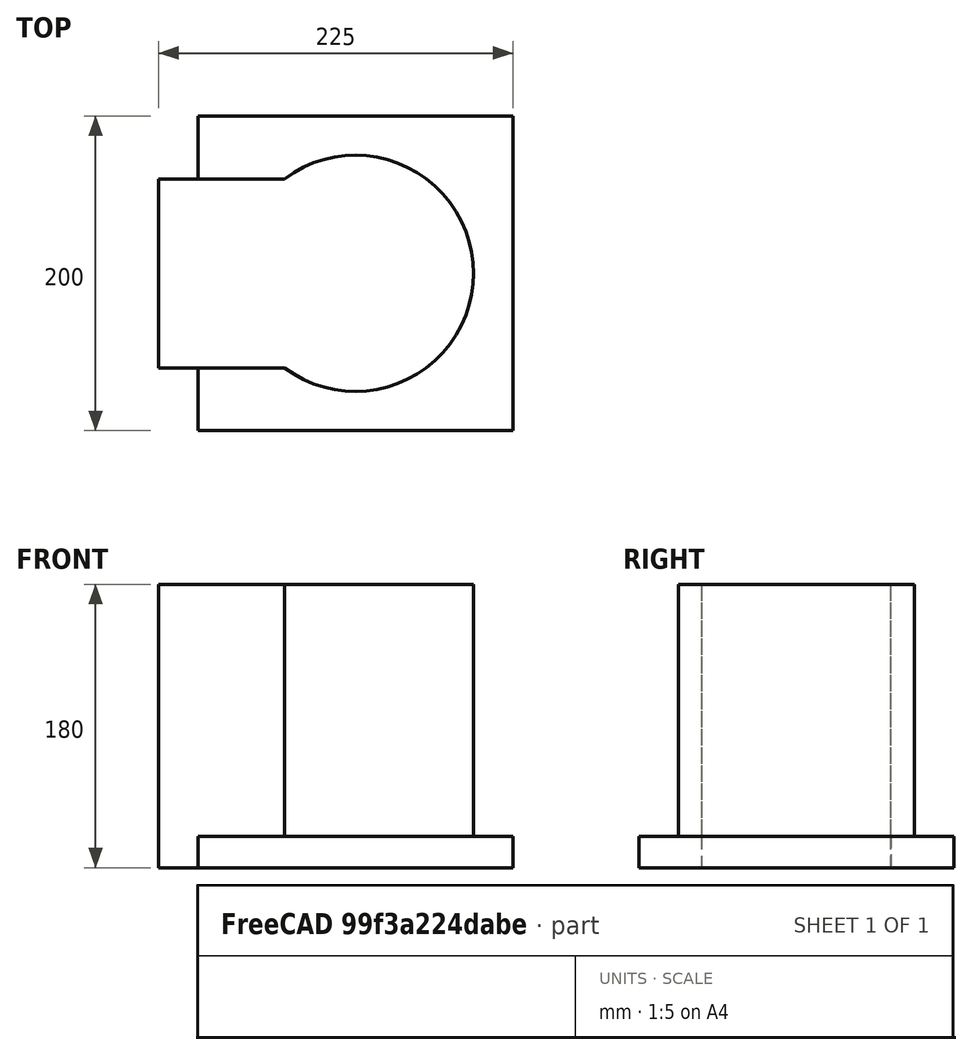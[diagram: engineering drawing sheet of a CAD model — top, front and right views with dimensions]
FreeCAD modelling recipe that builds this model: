
FCSTD DOCUMENT  (FreeCAD 0.19R)
Label: lk0
License: All rights reserved
LicenseURL: http://en.wikipedia.org/wiki/All_rights_reserved
objects: Sketcher::SketchObject×2, PartDesign::Pad×2, PartDesign::Body×1, Mesh::Feature×1
note: 7 computed .brp shape members not serialized (recipe doc carries the construction recipe); baked Part::Feature solids carry a one-line shape summary decoded from their .brp

FEATURE [Sketcher::SketchObject] Sketch
  FullyConstrained = true
  MapMode = 5
  Support = -> [XY_Plane]
  sketch-geometry (4):
    g0: ArcOfCircle CenterX=0 CenterY=0 CenterZ=0 NormalX=0 NormalY=0 NormalZ=1 AngleXU=0 Radius=75 StartAngle=4.06889 EndAngle=8.49748
    g1: LineSegment StartX=-45 StartY=60 StartZ=0 EndX=-125 EndY=60 EndZ=0
    g2: LineSegment StartX=-125 StartY=60 StartZ=0 EndX=-125 EndY=-60 EndZ=0
    g3: LineSegment StartX=-125 StartY=-60 StartZ=0 EndX=-45 EndY=-60 EndZ=0
  constraints (11):
    c: Coincident(g0,g-1)
    c: Diameter(g0) = 150
    c: Coincident(g1,g2)
    c: Coincident(g2,g3)
    c: Horizontal(g1)
    c: Horizontal(g3)
    c: DistanceY(g2,g2) = 120
    c: Symmetric(g1,g2,g-1)
    c: Coincident(g0,g3)
    c: Coincident(g0,g1)
    c: DistanceX(g1,g1) = 80
FEATURE [PartDesign::Pad] Pad
  Direction = (1,1,1)
  Length = 180
  Length2 = 100
  Profile = -> Sketch
  Type = 0
FEATURE [Sketcher::SketchObject] Sketch001
  FullyConstrained = true
  MapMode = 5
  Support = -> [XY_Plane]
  sketch-geometry (4):
    g0: LineSegment StartX=-100 StartY=100 StartZ=0 EndX=100 EndY=100 EndZ=0
    g1: LineSegment StartX=100 StartY=100 StartZ=0 EndX=100 EndY=-100 EndZ=0
    g2: LineSegment StartX=100 StartY=-100 StartZ=0 EndX=-100 EndY=-100 EndZ=0
    g3: LineSegment StartX=-100 StartY=-100 StartZ=0 EndX=-100 EndY=100 EndZ=0
  constraints (11):
    c: Coincident(g0,g1)
    c: Coincident(g1,g2)
    c: Coincident(g2,g3)
    c: Coincident(g3,g0)
    c: Horizontal(g0)
    c: Horizontal(g2)
    c: Vertical(g1)
    c: Vertical(g3)
    c: Equal(g1,g0)
    c: Symmetric(g1,g0,g-1)
    c: DistanceX(g2,g2) = 200
FEATURE [PartDesign::Pad] Pad001
  BaseFeature = -> Pad
  Direction = (1,1,1)
  Length = 20
  Length2 = 100
  Profile = -> Sketch001
  Type = 0
FEATURE [PartDesign::Body] Body
  Group = -> [Sketch,Pad,Sketch001,Pad001]
  Origin = -> Origin
  Tip = -> Pad001
FEATURE [Mesh::Feature] Mesh  label="Body (Meshed)"
